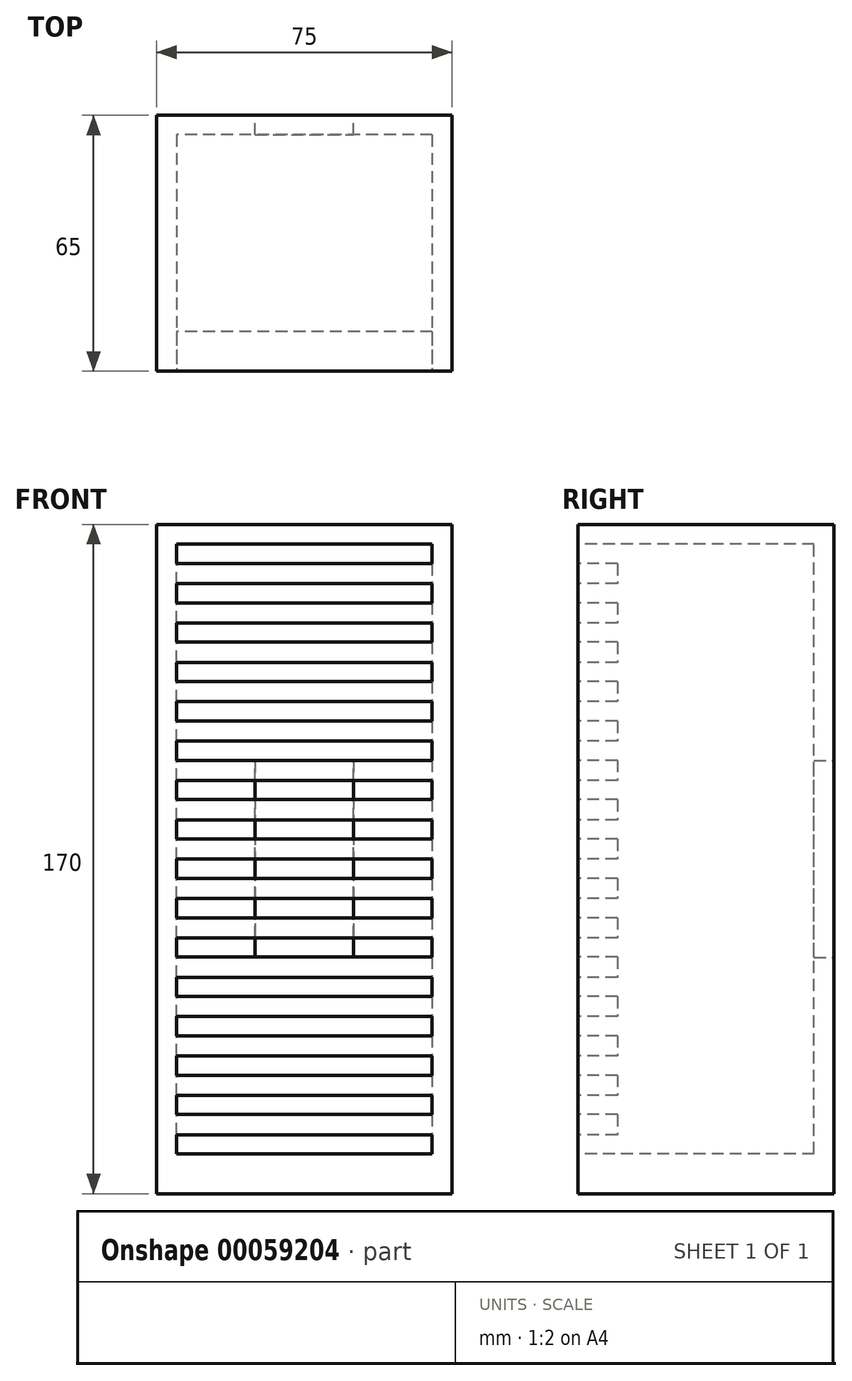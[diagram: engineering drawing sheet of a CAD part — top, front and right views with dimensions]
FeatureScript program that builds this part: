
annotation { "Feature Type Name" : "Feature", "Feature Type Description" : "" }
export const myFeature = defineFeature(function(context is Context, id is Id, definition is map)
    precondition{}
    {
        {
            var Q0;
            Q0=qCreatedBy(makeId("Right.planeOp"),FACE);
            var sketch = newSketch(context, id + "F0", { "sketchPlane" : qUnion([Q0])});
            skLineSegment(sketch, "E0", {"start": v(-41.76, 67.65) * mm, "end": v(-41.76, -102.35) * mm});
            skLineSegment(sketch, "E1", {"start": v(-41.76, -102.35) * mm, "end": v(-31.76, -102.35) * mm});
            skLineSegment(sketch, "E2", {"start": v(-31.76, -102.35) * mm, "end": v(-31.76, 67.65) * mm});
            skLineSegment(sketch, "E3", {"start": v(-31.76, 67.65) * mm, "end": v(-41.76, 67.65) * mm});
            skSolve(sketch);
        }
        {
            var Q0;
            Q0 = qSketchRegion(id + "F0", true);
            extrude(context, id + "F1", {"entities" : qUnion([Q0]), "endBound" : BoundingType.SYMMETRIC, "depth" : 75 * mm});
        }
        {
            var Q0;
            Q0=makeQuery(id+"F1.opExtrude","SWEPT_FACE",FACE,{"disambiguationData":[OSD([sQuery(id+"F0.wireOp",EDGE,"E0")])]});
            var sketch = newSketch(context, id + "F2", { "sketchPlane" : qUnion([Q0])});
            skLineSegment(sketch, "E4.bottom", {"start": v(-32.5, 62.65) * mm, "end": v(32.5, 62.65) * mm});
            skLineSegment(sketch, "E4.top", {"start": v(-32.5, 57.75) * mm, "end": v(32.5, 57.75) * mm});
            skLineSegment(sketch, "E4.left", {"start": v(-32.5, 62.65) * mm, "end": v(-32.5, 57.75) * mm});
            skLineSegment(sketch, "E4.right", {"start": v(32.5, 62.65) * mm, "end": v(32.5, 57.75) * mm});
            skLineSegment(sketch, "E5.0.1.0", {"start": v(-32.5, 52.65) * mm, "end": v(32.5, 52.65) * mm});
            skLineSegment(sketch, "E5.0.1.1", {"start": v(-32.5, 52.65) * mm, "end": v(-32.5, 47.75) * mm});
            skLineSegment(sketch, "E5.0.1.2", {"start": v(-32.5, 47.75) * mm, "end": v(32.5, 47.75) * mm});
            skLineSegment(sketch, "E5.0.1.3", {"start": v(32.5, 52.65) * mm, "end": v(32.5, 47.75) * mm});
            skLineSegment(sketch, "E5.0.2.0", {"start": v(-32.5, 42.65) * mm, "end": v(32.5, 42.65) * mm});
            skLineSegment(sketch, "E5.0.2.1", {"start": v(-32.5, 42.65) * mm, "end": v(-32.5, 37.75) * mm});
            skLineSegment(sketch, "E5.0.2.2", {"start": v(-32.5, 37.75) * mm, "end": v(32.5, 37.75) * mm});
            skLineSegment(sketch, "E5.0.2.3", {"start": v(32.5, 42.65) * mm, "end": v(32.5, 37.75) * mm});
            skLineSegment(sketch, "E5.0.3.0", {"start": v(-32.5, 32.65) * mm, "end": v(32.5, 32.65) * mm});
            skLineSegment(sketch, "E5.0.3.1", {"start": v(-32.5, 32.65) * mm, "end": v(-32.5, 27.75) * mm});
            skLineSegment(sketch, "E5.0.3.2", {"start": v(-32.5, 27.75) * mm, "end": v(32.5, 27.75) * mm});
            skLineSegment(sketch, "E5.0.3.3", {"start": v(32.5, 32.65) * mm, "end": v(32.5, 27.75) * mm});
            skLineSegment(sketch, "E5.0.4.0", {"start": v(-32.5, 22.65) * mm, "end": v(32.5, 22.65) * mm});
            skLineSegment(sketch, "E5.0.4.1", {"start": v(-32.5, 22.65) * mm, "end": v(-32.5, 17.75) * mm});
            skLineSegment(sketch, "E5.0.4.2", {"start": v(-32.5, 17.75) * mm, "end": v(32.5, 17.75) * mm});
            skLineSegment(sketch, "E5.0.4.3", {"start": v(32.5, 22.65) * mm, "end": v(32.5, 17.75) * mm});
            skLineSegment(sketch, "E5.direction1", {"start": v(-32.5, 62.65) * mm, "end": v(-7.5, 62.65) * mm, "construction": true});
            skLineSegment(sketch, "E5.direction2", {"start": v(-32.5, 62.65) * mm, "end": v(-32.5, 52.65) * mm, "construction": true});
            skLineSegment(sketch, "E6.0.0.5", {"start": v(-32.5, 12.65) * mm, "end": v(32.5, 12.65) * mm});
            skLineSegment(sketch, "E6.3.0.5", {"start": v(-32.5, 12.65) * mm, "end": v(-32.5, 7.75) * mm});
            skLineSegment(sketch, "E6.6.0.5", {"start": v(-32.5, 7.75) * mm, "end": v(32.5, 7.75) * mm});
            skLineSegment(sketch, "E6.9.0.5", {"start": v(32.5, 12.65) * mm, "end": v(32.5, 7.75) * mm});
            skLineSegment(sketch, "E6.0.0.6", {"start": v(-32.5, 2.65) * mm, "end": v(32.5, 2.65) * mm});
            skLineSegment(sketch, "E6.3.0.6", {"start": v(-32.5, 2.65) * mm, "end": v(-32.5, -2.25) * mm});
            skLineSegment(sketch, "E6.6.0.6", {"start": v(-32.5, -2.25) * mm, "end": v(32.5, -2.25) * mm});
            skLineSegment(sketch, "E6.9.0.6", {"start": v(32.5, 2.65) * mm, "end": v(32.5, -2.25) * mm});
            skLineSegment(sketch, "E6.0.0.7", {"start": v(-32.5, -7.35) * mm, "end": v(32.5, -7.35) * mm});
            skLineSegment(sketch, "E6.3.0.7", {"start": v(-32.5, -7.35) * mm, "end": v(-32.5, -12.25) * mm});
            skLineSegment(sketch, "E6.6.0.7", {"start": v(-32.5, -12.25) * mm, "end": v(32.5, -12.25) * mm});
            skLineSegment(sketch, "E6.9.0.7", {"start": v(32.5, -7.35) * mm, "end": v(32.5, -12.25) * mm});
            skLineSegment(sketch, "E7.0.0.8", {"start": v(-32.5, -17.35) * mm, "end": v(32.5, -17.35) * mm});
            skLineSegment(sketch, "E7.3.0.8", {"start": v(-32.5, -17.35) * mm, "end": v(-32.5, -22.25) * mm});
            skLineSegment(sketch, "E7.6.0.8", {"start": v(-32.5, -22.25) * mm, "end": v(32.5, -22.25) * mm});
            skLineSegment(sketch, "E7.9.0.8", {"start": v(32.5, -17.35) * mm, "end": v(32.5, -22.25) * mm});
            skLineSegment(sketch, "E7.0.0.9", {"start": v(-32.5, -27.35) * mm, "end": v(32.5, -27.35) * mm});
            skLineSegment(sketch, "E7.3.0.9", {"start": v(-32.5, -27.35) * mm, "end": v(-32.5, -32.25) * mm});
            skLineSegment(sketch, "E7.6.0.9", {"start": v(-32.5, -32.25) * mm, "end": v(32.5, -32.25) * mm});
            skLineSegment(sketch, "E7.9.0.9", {"start": v(32.5, -27.35) * mm, "end": v(32.5, -32.25) * mm});
            skLineSegment(sketch, "E7.0.0.10", {"start": v(-32.5, -37.35) * mm, "end": v(32.5, -37.35) * mm});
            skLineSegment(sketch, "E7.3.0.10", {"start": v(-32.5, -37.35) * mm, "end": v(-32.5, -42.25) * mm});
            skLineSegment(sketch, "E7.6.0.10", {"start": v(-32.5, -42.25) * mm, "end": v(32.5, -42.25) * mm});
            skLineSegment(sketch, "E7.9.0.10", {"start": v(32.5, -37.35) * mm, "end": v(32.5, -42.25) * mm});
            skLineSegment(sketch, "E7.0.0.11", {"start": v(-32.5, -47.35) * mm, "end": v(32.5, -47.35) * mm});
            skLineSegment(sketch, "E7.3.0.11", {"start": v(-32.5, -47.35) * mm, "end": v(-32.5, -52.25) * mm});
            skLineSegment(sketch, "E7.6.0.11", {"start": v(-32.5, -52.25) * mm, "end": v(32.5, -52.25) * mm});
            skLineSegment(sketch, "E7.9.0.11", {"start": v(32.5, -47.35) * mm, "end": v(32.5, -52.25) * mm});
            skLineSegment(sketch, "E7.0.0.12", {"start": v(-32.5, -57.35) * mm, "end": v(32.5, -57.35) * mm});
            skLineSegment(sketch, "E7.3.0.12", {"start": v(-32.5, -57.35) * mm, "end": v(-32.5, -62.25) * mm});
            skLineSegment(sketch, "E7.6.0.12", {"start": v(-32.5, -62.25) * mm, "end": v(32.5, -62.25) * mm});
            skLineSegment(sketch, "E7.9.0.12", {"start": v(32.5, -57.35) * mm, "end": v(32.5, -62.25) * mm});
            skLineSegment(sketch, "E7.0.0.13", {"start": v(-32.5, -67.35) * mm, "end": v(32.5, -67.35) * mm});
            skLineSegment(sketch, "E7.3.0.13", {"start": v(-32.5, -67.35) * mm, "end": v(-32.5, -72.25) * mm});
            skLineSegment(sketch, "E7.6.0.13", {"start": v(-32.5, -72.25) * mm, "end": v(32.5, -72.25) * mm});
            skLineSegment(sketch, "E7.9.0.13", {"start": v(32.5, -67.35) * mm, "end": v(32.5, -72.25) * mm});
            skLineSegment(sketch, "E7.0.0.14", {"start": v(-32.5, -77.35) * mm, "end": v(32.5, -77.35) * mm});
            skLineSegment(sketch, "E7.3.0.14", {"start": v(-32.5, -77.35) * mm, "end": v(-32.5, -82.25) * mm});
            skLineSegment(sketch, "E7.6.0.14", {"start": v(-32.5, -82.25) * mm, "end": v(32.5, -82.25) * mm});
            skLineSegment(sketch, "E7.9.0.14", {"start": v(32.5, -77.35) * mm, "end": v(32.5, -82.25) * mm});
            skLineSegment(sketch, "E7.0.0.15", {"start": v(-32.5, -87.35) * mm, "end": v(32.5, -87.35) * mm});
            skLineSegment(sketch, "E7.3.0.15", {"start": v(-32.5, -87.35) * mm, "end": v(-32.5, -92.25) * mm});
            skLineSegment(sketch, "E7.6.0.15", {"start": v(-32.5, -92.25) * mm, "end": v(32.5, -92.25) * mm});
            skLineSegment(sketch, "E7.9.0.15", {"start": v(32.5, -87.35) * mm, "end": v(32.5, -92.25) * mm});
            skSolve(sketch);
        }
        {
            var Q0;
            Q0 = qSketchRegion(id + "F2", true);
            extrude(context, id + "F3", {"entities" : qUnion([Q0]), "operationType" : NewBodyOperationType.REMOVE, "endBound" : BoundingType.UP_TO_NEXT, "oppositeDirection" : true, "depth" : 25 * mm});
        }
        {
            var Q0;
            Q0=makeQuery(id+"F1.opExtrude","SWEPT_FACE",FACE,{"disambiguationData":[OSD([sQuery(id+"F0.wireOp",EDGE,"E2")])]});
            var sketch = newSketch(context, id + "F4", { "sketchPlane" : qUnion([Q0])});
            skLineSegment(sketch, "E8", {"start": v(37.5, 67.65) * mm, "end": v(-37.5, 67.65) * mm});
            skLineSegment(sketch, "E9", {"start": v(-37.5, 67.65) * mm, "end": v(-37.5, -102.35) * mm});
            skLineSegment(sketch, "E10", {"start": v(-37.5, -102.35) * mm, "end": v(37.5, -102.35) * mm});
            skLineSegment(sketch, "E11", {"start": v(37.5, -102.35) * mm, "end": v(37.5, 67.65) * mm});
            skLineSegment(sketch, "E12", {"start": v(32.5, 62.65) * mm, "end": v(-32.5, 62.65) * mm});
            skLineSegment(sketch, "E13", {"start": v(-32.5, 62.65) * mm, "end": v(-32.5, -92.25) * mm});
            skLineSegment(sketch, "E14", {"start": v(-32.5, -92.25) * mm, "end": v(32.5, -92.25) * mm});
            skLineSegment(sketch, "E15", {"start": v(32.5, -92.25) * mm, "end": v(32.5, 62.65) * mm});
            skSolve(sketch);
        }
        {
            var Q0;
            Q0 = qSketchRegion(id + "F4", true);
            extrude(context, id + "F5", {"entities" : qUnion([Q0]), "operationType" : NewBodyOperationType.ADD, "depth" : 50 * mm});
        }
        {
            var Q0;
            Q0=makeQuery(id+"F5.opExtrude","CAP_FACE",FACE,{"disambiguationData":[OSD([sQuery(id+"F4.wireOp",EDGE,"E8"),sQuery(id+"F4.wireOp",EDGE,"E9"),sQuery(id+"F4.wireOp",EDGE,"E10"),sQuery(id+"F4.wireOp",EDGE,"E11"),sQuery(id+"F4.wireOp",EDGE,"E12"),sQuery(id+"F4.wireOp",EDGE,"E13"),sQuery(id+"F4.wireOp",EDGE,"E14"),sQuery(id+"F4.wireOp",EDGE,"E15")])],"isStart":false});
            var sketch = newSketch(context, id + "F6", { "sketchPlane" : qUnion([Q0])});
            skLineSegment(sketch, "E16", {"start": v(-37.5, 67.65) * mm, "end": v(37.5, 67.65) * mm});
            skLineSegment(sketch, "E17", {"start": v(37.5, 67.65) * mm, "end": v(37.5, -102.35) * mm});
            skLineSegment(sketch, "E18", {"start": v(37.5, -102.35) * mm, "end": v(-37.5, -102.35) * mm});
            skLineSegment(sketch, "E19", {"start": v(-37.5, -102.35) * mm, "end": v(-37.5, 67.65) * mm});
            skSolve(sketch);
        }
        {
            var Q0;
            Q0 = qSketchRegion(id + "F6", true);
            extrude(context, id + "F7", {"entities" : qUnion([Q0]), "operationType" : NewBodyOperationType.ADD, "depth" : 5 * mm});
        }
        {
            var Q0;
            Q0=makeQuery(id+"F7.opExtrude","CAP_FACE",FACE,{"disambiguationData":[OSD([sQuery(id+"F6.wireOp",EDGE,"E16"),sQuery(id+"F6.wireOp",EDGE,"E17"),sQuery(id+"F6.wireOp",EDGE,"E18"),sQuery(id+"F6.wireOp",EDGE,"E19")])],"isStart":false});
            var sketch = newSketch(context, id + "F8", { "sketchPlane" : qUnion([Q0])});
            skLineSegment(sketch, "E20.bottom", {"start": v(-12.5, 7.65) * mm, "end": v(12.5, 7.65) * mm});
            skLineSegment(sketch, "E20.top", {"start": v(-12.5, -42.35) * mm, "end": v(12.5, -42.35) * mm});
            skLineSegment(sketch, "E20.left", {"start": v(-12.5, 7.65) * mm, "end": v(-12.5, -42.35) * mm});
            skLineSegment(sketch, "E20.right", {"start": v(12.5, 7.65) * mm, "end": v(12.5, -42.35) * mm});
            skLineSegment(sketch, "E21", {"start": v(0, 67.65) * mm, "end": v(0, -102.35) * mm, "construction": true});
            skLineSegment(sketch, "E22", {"start": v(-37.5, -17.35) * mm, "end": v(37.5, -17.35) * mm, "construction": true});
            skSolve(sketch);
        }
        {
            var Q0;
            Q0 = qSketchRegion(id + "F8", true);
            extrude(context, id + "F9", {"entities" : qUnion([Q0]), "operationType" : NewBodyOperationType.REMOVE, "endBound" : BoundingType.UP_TO_NEXT, "oppositeDirection" : true, "depth" : 25 * mm});
        }
    });
